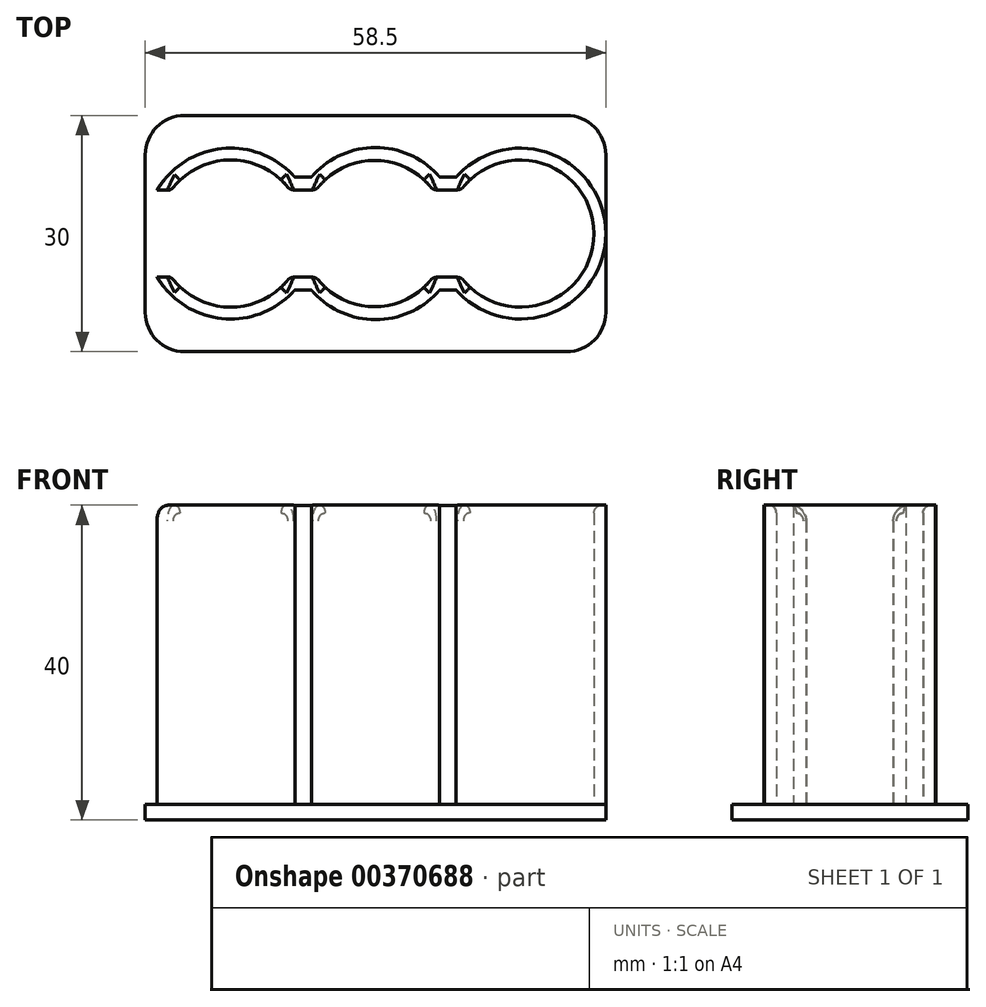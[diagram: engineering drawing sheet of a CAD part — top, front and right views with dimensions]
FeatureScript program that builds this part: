
annotation { "Feature Type Name" : "Feature", "Feature Type Description" : "" }
export const myFeature = defineFeature(function(context is Context, id is Id, definition is map)
    precondition{}
    {
        {
            var Q0;
            Q0=qCreatedBy(makeId("Top.planeOp"),FACE);
            var sketch = newSketch(context, id + "F0", { "sketchPlane" : qUnion([Q0])});
            skArc(sketch, "E0", {"start": v(7.52, 5.55) * mm, "mid": v(-9.35, 0) * mm, "end": v(7.52, -5.55) * mm});
            skArc(sketch, "E1.2.0.0", {"start": v(29.28, -5.55) * mm, "mid": v(46.15, 0) * mm, "end": v(29.28, 5.55) * mm});
            skLineSegment(sketch, "E1.direction1", {"start": v(0, 0) * mm, "end": v(18.5, 0) * mm, "construction": true});
            skArc(sketch, "E2.0", {"start": v(8.15, 7.16) * mm, "mid": v(-10.85, 0) * mm, "end": v(8.15, -7.16) * mm});
            skArc(sketch, "E3.0", {"start": v(28.65, -7.16) * mm, "mid": v(47.65, 0) * mm, "end": v(28.65, 7.16) * mm});
            skLineSegment(sketch, "E4", {"start": v(8.15, 7.16) * mm, "end": v(10.25, 7.16) * mm});
            skLineSegment(sketch, "E5.1.0.0", {"start": v(26.55, 7.16) * mm, "end": v(28.65, 7.16) * mm});
            skLineSegment(sketch, "E5.direction1", {"start": v(8.15, 7.16) * mm, "end": v(10.25, 7.16) * mm, "construction": true});
            skLineSegment(sketch, "E6", {"start": v(9.2, 5.55) * mm, "end": v(7.52, 5.55) * mm});
            skLineSegment(sketch, "E7", {"start": v(7.52, 5.55) * mm, "end": v(10.88, 5.55) * mm});
            skLineSegment(sketch, "E8.MirrorCS", {"start": v(8.15, -7.16) * mm, "end": v(10.25, -7.16) * mm});
            skLineSegment(sketch, "E9.MirrorCS", {"start": v(7.52, -5.55) * mm, "end": v(10.88, -5.55) * mm});
            skLineSegment(sketch, "E10.MirrorCS", {"start": v(26.55, -7.16) * mm, "end": v(28.65, -7.16) * mm});
            skLineSegment(sketch, "E11.MirrorCS", {"start": v(25.68, -5.55) * mm, "end": v(29.28, -5.55) * mm});
            skArc(sketch, "E12.trimOffspring", {"start": v(10.25, -7.16) * mm, "mid": v(18.4, -10.93) * mm, "end": v(26.55, -7.16) * mm});
            skArc(sketch, "E13.trimOffspring", {"start": v(10.88, -5.55) * mm, "mid": v(18.28, -9.29) * mm, "end": v(25.68, -5.55) * mm});
            skArc(sketch, "E14.trimOffspring", {"start": v(26.55, 7.16) * mm, "mid": v(18.4, 10.93) * mm, "end": v(10.25, 7.16) * mm});
            skArc(sketch, "E15.trimOffspring", {"start": v(25.68, 5.55) * mm, "mid": v(18.28, 9.29) * mm, "end": v(10.88, 5.55) * mm});
            skLineSegment(sketch, "E16", {"start": v(25.68, 5.55) * mm, "end": v(29.28, 5.55) * mm});
            skSolve(sketch);
        }
        {
            var Q0;
            {var subQ3=sQuery(id+"F0.wireOp",EDGE,"E0");Q0=makeQuery(id+"F0.imprint","IMPRINT",FACE,{"disambiguationData":[TD([[makeQuery(id+"F0.imprint","IMPRINT",EDGE,{"derivedFrom":subQ3}),-1.0]])]});}
            extrude(context, id + "F1", {"entities" : qUnion([Q0]), "depth" : 40 * mm});
        }
        {
            var Q0;
            Q0=qCreatedBy(makeId("Top.planeOp"),FACE);
            var sketch = newSketch(context, id + "F2", { "sketchPlane" : qUnion([Q0])});
            skLineSegment(sketch, "E17.bottom", {"start": v(-10.85, -15) * mm, "end": v(47.65, -15) * mm});
            skLineSegment(sketch, "E17.top", {"start": v(-10.85, 15) * mm, "end": v(47.65, 15) * mm});
            skLineSegment(sketch, "E17.left", {"start": v(-10.85, -15) * mm, "end": v(-10.85, 15) * mm});
            skLineSegment(sketch, "E17.right", {"start": v(47.65, -15) * mm, "end": v(47.65, 15) * mm});
            skPoint(sketch, "E17.middle", {"position": v(18.4, 0) * mm});
            skSolve(sketch);
        }
        {
            var Q0;
            Q0=makeQuery(id+"F2.imprint","IMPRINT",FACE,{"disambiguationData":[TD([[makeQuery(id+"F2.imprint","IMPRINT",EDGE,{"derivedFrom":sQuery(id+"F2.wireOp",EDGE,"E17.bottom")}),1.0]])]});
            extrude(context, id + "F3", {"entities" : qUnion([Q0]), "operationType" : NewBodyOperationType.ADD, "depth" : 2 * mm});
        }
        {
            var Q0;
            Q0=makeQuery(id+"F3.opExtrude","SWEPT_EDGE",EDGE,{"disambiguationData":[OSD([sQuery(id+"F2.wireOp",EDGE,"E17.bottom"),sQuery(id+"F2.wireOp",EDGE,"E17.left")])]});
            var Q1;
            Q1=makeQuery(id+"F3.opExtrude","SWEPT_EDGE",EDGE,{"disambiguationData":[OSD([sQuery(id+"F2.wireOp",EDGE,"E17.bottom"),sQuery(id+"F2.wireOp",EDGE,"E17.right")])]});
            var Q2;
            Q2=makeQuery(id+"F3.opExtrude","SWEPT_EDGE",EDGE,{"disambiguationData":[OSD([sQuery(id+"F2.wireOp",EDGE,"E17.top"),sQuery(id+"F2.wireOp",EDGE,"E17.left")])]});
            var Q3;
            Q3=makeQuery(id+"F3.opExtrude","SWEPT_EDGE",EDGE,{"disambiguationData":[OSD([sQuery(id+"F2.wireOp",EDGE,"E17.top"),sQuery(id+"F2.wireOp",EDGE,"E17.right")])]});
            fillet(context, id + "F4", {"entities" : qUnion([Q0, Q1, Q2, Q3]), "radius" : 5 * mm, "tangentPropagation" : true, "allowEdgeOverflow" : false});
        }
        {
            var Q0;
            Q0=qCreatedBy(makeId("Right.planeOp"),FACE);
            var sketch = newSketch(context, id + "F5", { "sketchPlane" : qUnion([Q0])});
            skLineSegment(sketch, "E18.bottom", {"start": v(-5.5, 2) * mm, "end": v(5.5, 2) * mm});
            skLineSegment(sketch, "E18.top", {"start": v(-5.5, 52) * mm, "end": v(5.5, 52) * mm});
            skLineSegment(sketch, "E18.left", {"start": v(-5.5, 2) * mm, "end": v(-5.5, 52) * mm});
            skLineSegment(sketch, "E18.right", {"start": v(5.5, 2) * mm, "end": v(5.5, 52) * mm});
            skPoint(sketch, "E18.middle", {"position": v(0, 27) * mm});
            skSolve(sketch);
        }
        {
            var Q0;
            Q0=makeQuery(id+"F5.imprint","IMPRINT",FACE,{"disambiguationData":[TD([[makeQuery(id+"F5.imprint","IMPRINT",EDGE,{"derivedFrom":sQuery(id+"F5.wireOp",EDGE,"E18.bottom")}),1.0]])]});
            extrude(context, id + "F6", {"entities" : qUnion([Q0]), "operationType" : NewBodyOperationType.REMOVE, "oppositeDirection" : true, "depth" : 25 * mm});
        }
        {
            var Q0;
            Q0=makeQuery(id+"F6.boolean.opBoolean","INTERSECT",EDGE,{"derivedFrom":[makeQuery(id+"F1.opExtrude","CAP_FACE",FACE,{"disambiguationData":[OSD([sQuery(id+"F0.wireOp",EDGE,"E0"),sQuery(id+"F0.wireOp",EDGE,"E1.2.0.0"),sQuery(id+"F0.wireOp",EDGE,"E2.0"),sQuery(id+"F0.wireOp",EDGE,"E3.0"),sQuery(id+"F0.wireOp",EDGE,"E4"),sQuery(id+"F0.wireOp",EDGE,"E5.1.0.0"),sQuery(id+"F0.wireOp",EDGE,"E7"),sQuery(id+"F0.wireOp",EDGE,"E8.MirrorCS"),sQuery(id+"F0.wireOp",EDGE,"E9.MirrorCS"),sQuery(id+"F0.wireOp",EDGE,"E10.MirrorCS"),sQuery(id+"F0.wireOp",EDGE,"E11.MirrorCS"),sQuery(id+"F0.wireOp",EDGE,"E12.trimOffspring"),sQuery(id+"F0.wireOp",EDGE,"E13.trimOffspring"),sQuery(id+"F0.wireOp",EDGE,"E14.trimOffspring"),sQuery(id+"F0.wireOp",EDGE,"E15.trimOffspring"),sQuery(id+"F0.wireOp",EDGE,"E16")])],"isStart":false}),makeQuery(id+"F6.opExtrude","SWEPT_FACE",FACE,{"disambiguationData":[OSD([sQuery(id+"F5.wireOp",EDGE,"E18.right")])]})]});
            var Q1;
            Q1=makeQuery(id+"F1.opExtrude","CAP_EDGE",EDGE,{"disambiguationData":[OSD([sQuery(id+"F0.wireOp",EDGE,"E7")])],"isStart":false});
            var Q2;
            Q2=makeQuery(id+"F1.opExtrude","CAP_EDGE",EDGE,{"disambiguationData":[OSD([sQuery(id+"F0.wireOp",EDGE,"E16")])],"isStart":false});
            var Q3;
            Q3=makeQuery(id+"F1.opExtrude","CAP_EDGE",EDGE,{"disambiguationData":[OSD([sQuery(id+"F0.wireOp",EDGE,"E11.MirrorCS")])],"isStart":false});
            var Q4;
            Q4=makeQuery(id+"F1.opExtrude","CAP_EDGE",EDGE,{"disambiguationData":[OSD([sQuery(id+"F0.wireOp",EDGE,"E9.MirrorCS")])],"isStart":false});
            var Q5;
            Q5=makeQuery(id+"F6.boolean.opBoolean","INTERSECT",EDGE,{"derivedFrom":[makeQuery(id+"F1.opExtrude","CAP_FACE",FACE,{"disambiguationData":[OSD([sQuery(id+"F0.wireOp",EDGE,"E0"),sQuery(id+"F0.wireOp",EDGE,"E1.2.0.0"),sQuery(id+"F0.wireOp",EDGE,"E2.0"),sQuery(id+"F0.wireOp",EDGE,"E3.0"),sQuery(id+"F0.wireOp",EDGE,"E4"),sQuery(id+"F0.wireOp",EDGE,"E5.1.0.0"),sQuery(id+"F0.wireOp",EDGE,"E7"),sQuery(id+"F0.wireOp",EDGE,"E8.MirrorCS"),sQuery(id+"F0.wireOp",EDGE,"E9.MirrorCS"),sQuery(id+"F0.wireOp",EDGE,"E10.MirrorCS"),sQuery(id+"F0.wireOp",EDGE,"E11.MirrorCS"),sQuery(id+"F0.wireOp",EDGE,"E12.trimOffspring"),sQuery(id+"F0.wireOp",EDGE,"E13.trimOffspring"),sQuery(id+"F0.wireOp",EDGE,"E14.trimOffspring"),sQuery(id+"F0.wireOp",EDGE,"E15.trimOffspring"),sQuery(id+"F0.wireOp",EDGE,"E16")])],"isStart":false}),makeQuery(id+"F6.opExtrude","SWEPT_FACE",FACE,{"disambiguationData":[OSD([sQuery(id+"F5.wireOp",EDGE,"E18.left")])]})]});
            fillet(context, id + "F7", {"entities" : qUnion([Q0, Q1, Q2, Q3, Q4, Q5]), "radius" : 2 * mm, "tangentPropagation" : true, "allowEdgeOverflow" : false});
        }
        {
            var Q0;
            {var subQ0=sQuery(id+"F0.wireOp",EDGE,"E0");var subQ1=sQuery(id+"F0.wireOp",EDGE,"E7");Q0=makeQuery(id+"F6.boolean.opBoolean","SPLIT",EDGE,{"disambiguationData":[TD([makeQuery(id+"F1.opExtrude","SWEPT_FACE",FACE,{"disambiguationData":[OSD([subQ1])]})])],"derivedFrom":makeQuery(id+"F1.opExtrude","CAP_EDGE",EDGE,{"disambiguationData":[OSD([subQ0])],"isStart":false})});}
            var Q1;
            Q1=makeQuery(id+"F1.opExtrude","CAP_EDGE",EDGE,{"disambiguationData":[OSD([sQuery(id+"F0.wireOp",EDGE,"E15.trimOffspring")])],"isStart":false});
            var Q2;
            Q2=makeQuery(id+"F1.opExtrude","CAP_EDGE",EDGE,{"disambiguationData":[OSD([sQuery(id+"F0.wireOp",EDGE,"E1.2.0.0")])],"isStart":false});
            var Q3;
            Q3=makeQuery(id+"F1.opExtrude","CAP_EDGE",EDGE,{"disambiguationData":[OSD([sQuery(id+"F0.wireOp",EDGE,"E13.trimOffspring")])],"isStart":false});
            var Q4;
            {var subQ0=sQuery(id+"F0.wireOp",EDGE,"E0");var subQ1=sQuery(id+"F0.wireOp",EDGE,"E9.MirrorCS");Q4=makeQuery(id+"F6.boolean.opBoolean","SPLIT",EDGE,{"disambiguationData":[TD([makeQuery(id+"F1.opExtrude","SWEPT_FACE",FACE,{"disambiguationData":[OSD([subQ1])]})])],"derivedFrom":makeQuery(id+"F1.opExtrude","CAP_EDGE",EDGE,{"disambiguationData":[OSD([subQ0])],"isStart":false})});}
            fillet(context, id + "F8", {"entities" : qUnion([Q0, Q1, Q2, Q3, Q4]), "radius" : 1 * mm, "tangentPropagation" : true, "allowEdgeOverflow" : false});
        }
    });
